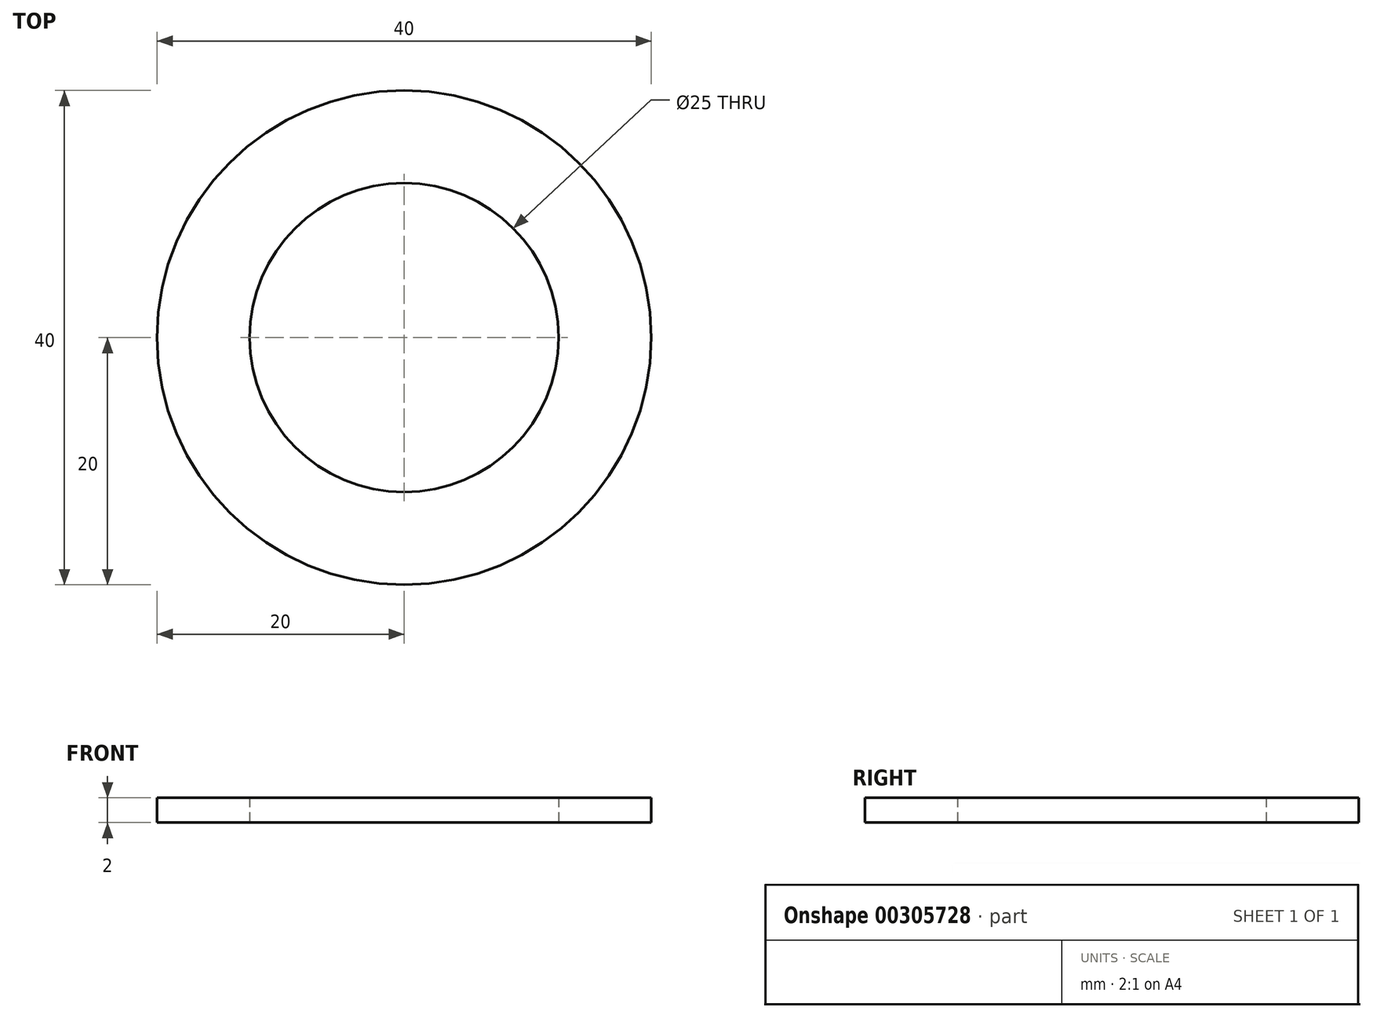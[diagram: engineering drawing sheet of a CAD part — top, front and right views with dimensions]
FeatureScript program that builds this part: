
annotation { "Feature Type Name" : "Feature", "Feature Type Description" : "" }
export const myFeature = defineFeature(function(context is Context, id is Id, definition is map)
    precondition{}
    {
        {
            var Q0;
            Q0=qCreatedBy(makeId("Top.planeOp"),FACE);
            var sketch = newSketch(context, id + "F0", { "sketchPlane" : qUnion([Q0])});
            skCircle(sketch, "E0", {"center": v(0, 0) * mm, "radius": 20 * mm});
            skCircle(sketch, "E1", {"center": v(0, 0) * mm, "radius": 12.5 * mm});
            skSolve(sketch);
        }
        {
            var Q0;
            Q0=qSketchRegion(id+"F0",true);
            extrude(context, id + "F1", {"entities" : qUnion([Q0]), "depth" : 2 * mm});
        }
    });
